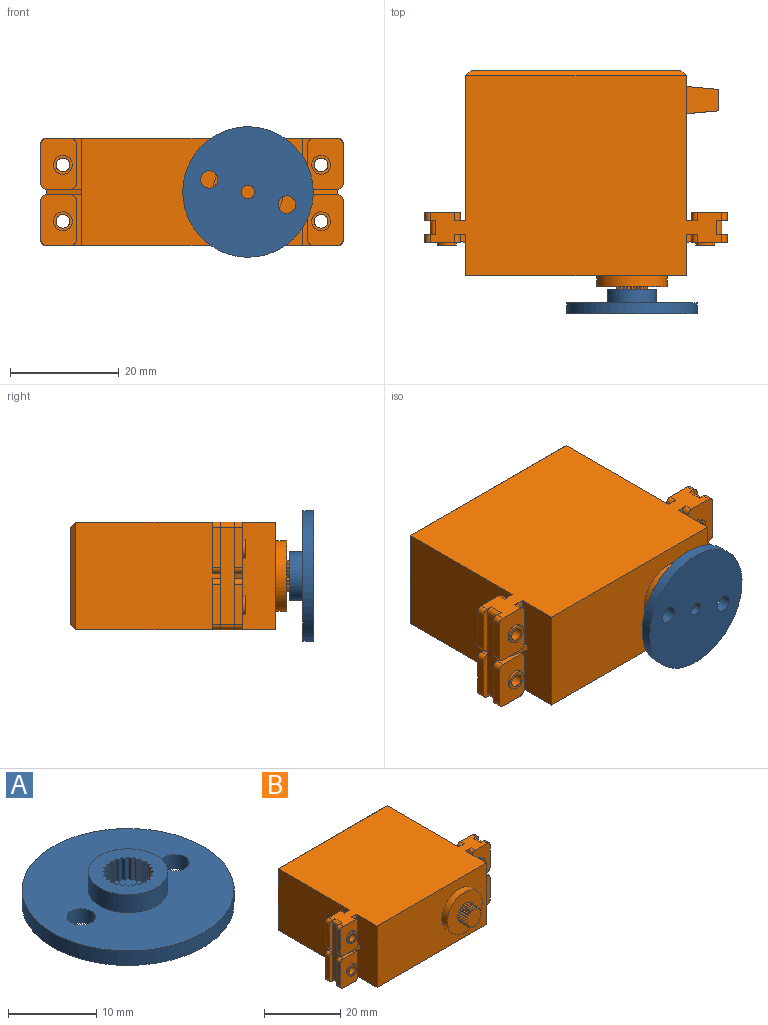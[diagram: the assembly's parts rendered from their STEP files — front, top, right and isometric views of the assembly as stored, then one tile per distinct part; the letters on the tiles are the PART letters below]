
ASSEMBLY  parts=2 mates=1
PART A: 57 faces, bbox 24x24x4.5 mm
  f0: plane 9x9mm, normal (0,0,1), area 40.5mm2, adj f4,f6,f7,f8,f9,f10,f11,f12
  f1: cylinder r=12mm len=24mm, axis (0,0,-1), area 150.8mm2, adj f2,f3
  f2: plane 24x24mm, normal (0,0,1), area 372.7mm2, adj f1,f4,f55,f56
  f3: plane 24x24mm, normal (0,0,-1), area 431.4mm2, adj f1,f54,f55,f56
  f4: cylinder r=4.5mm len=9mm, axis (0,0,-1), area 70.7mm2, adj f0,f2
  f5: plane 5.76x5.76mm, normal (0,0,1), area 18.2mm2, adj f6,f7,f8,f9,f10,f11,f12,f13
  f6: plane 3x0.34mm, normal (-0.71,-0.7,0), area 1.4mm2, adj f0,f5,f7,f9
  f7: plane 3x0.34mm, normal (0.71,-0.7,0), area 1.4mm2, adj f0,f5,f6,f52
  f8: plane 3x0.41mm, normal (-0.87,-0.5,0), area 1.4mm2, adj f0,f5,f9,f11
  f9: plane 3x0.41mm, normal (0.5,-0.86,0), area 1.4mm2, adj f0,f5,f6,f8
  f10: plane 3x0.46mm, normal (-0.97,-0.26,0), area 1.4mm2, adj f0,f5,f11,f13
  f11: plane 3x0.46mm, normal (0.26,-0.97,0), area 1.4mm2, adj f0,f5,f8,f10
  f12: plane 3x0.48mm, normal (-1,0,0), area 1.4mm2, adj f0,f5,f13,f15
  f13: plane 3x0.48mm, normal (0,-1,0), area 1.4mm2, adj f0,f5,f10,f12
  f14: plane 3x0.46mm, normal (-0.97,0.26,0), area 1.4mm2, adj f0,f5,f15,f17
  f15: plane 3x0.46mm, normal (-0.26,-0.97,0), area 1.4mm2, adj f0,f5,f12,f14
  f16: plane 3x0.41mm, normal (-0.86,0.5,0), area 1.4mm2, adj f0,f5,f17,f19
  f17: plane 3x0.41mm, normal (-0.5,-0.87,0), area 1.4mm2, adj f0,f5,f14,f16
  f18: plane 3x0.34mm, normal (-0.7,0.71,0), area 1.4mm2, adj f0,f5,f19,f21
  f19: plane 3x0.34mm, normal (-0.7,-0.71,0), area 1.4mm2, adj f0,f5,f16,f18
  f20: plane 3x0.41mm, normal (-0.5,0.87,0), area 1.4mm2, adj f0,f5,f21,f23
  f21: plane 3x0.41mm, normal (-0.86,-0.5,0), area 1.4mm2, adj f0,f5,f18,f20
  f22: plane 3x0.46mm, normal (-0.26,0.97,0), area 1.4mm2, adj f0,f5,f23,f25
  f23: plane 3x0.46mm, normal (-0.97,-0.26,0), area 1.4mm2, adj f0,f5,f20,f22
  f24: plane 3x0.48mm, normal (0,1,0), area 1.4mm2, adj f0,f5,f25,f27
  f25: plane 3x0.48mm, normal (-1,0,0), area 1.4mm2, adj f0,f5,f22,f24
  f26: plane 3x0.46mm, normal (0.26,0.97,0), area 1.4mm2, adj f0,f5,f27,f29
  f27: plane 3x0.46mm, normal (-0.97,0.26,0), area 1.4mm2, adj f0,f5,f24,f26
  f28: plane 3x0.41mm, normal (0.5,0.86,0), area 1.4mm2, adj f0,f5,f29,f31
  f29: plane 3x0.41mm, normal (-0.87,0.5,0), area 1.4mm2, adj f0,f5,f26,f28
  f30: plane 3x0.34mm, normal (0.71,0.7,0), area 1.4mm2, adj f0,f5,f31,f33
  f31: plane 3x0.34mm, normal (-0.71,0.7,0), area 1.4mm2, adj f0,f5,f28,f30
  f32: plane 3x0.41mm, normal (0.87,0.5,0), area 1.4mm2, adj f0,f5,f33,f35
  f33: plane 3x0.41mm, normal (-0.5,0.86,0), area 1.4mm2, adj f0,f5,f30,f32
  f34: plane 3x0.46mm, normal (0.97,0.26,0), area 1.4mm2, adj f0,f5,f35,f37
  f35: plane 3x0.46mm, normal (-0.26,0.97,0), area 1.4mm2, adj f0,f5,f32,f34
  f36: plane 3x0.48mm, normal (1,0,0), area 1.4mm2, adj f0,f5,f37,f39
  f37: plane 3x0.48mm, normal (0,1,0), area 1.4mm2, adj f0,f5,f34,f36
  f38: plane 3x0.46mm, normal (0.97,-0.26,0), area 1.4mm2, adj f0,f5,f39,f41
  f39: plane 3x0.46mm, normal (0.26,0.97,0), area 1.4mm2, adj f0,f5,f36,f38
  f40: plane 3x0.41mm, normal (0.86,-0.5,0), area 1.4mm2, adj f0,f5,f41,f43
  f41: plane 3x0.41mm, normal (0.5,0.87,0), area 1.4mm2, adj f0,f5,f38,f40
  f42: plane 3x0.34mm, normal (0.7,-0.71,0), area 1.4mm2, adj f0,f5,f43,f45
  f43: plane 3x0.34mm, normal (0.7,0.71,0), area 1.4mm2, adj f0,f5,f40,f42
  f44: plane 3x0.41mm, normal (0.5,-0.87,0), area 1.4mm2, adj f0,f5,f45,f47
  f45: plane 3x0.41mm, normal (0.86,0.5,0), area 1.4mm2, adj f0,f5,f42,f44
  f46: plane 3x0.46mm, normal (0.26,-0.97,0), area 1.4mm2, adj f0,f5,f47,f49
  f47: plane 3x0.46mm, normal (0.97,0.26,0), area 1.4mm2, adj f0,f5,f44,f46
  f48: plane 3x0.48mm, normal (0,-1,0), area 1.4mm2, adj f0,f5,f49,f51
  f49: plane 3x0.48mm, normal (1,0,0), area 1.4mm2, adj f0,f5,f46,f48
  f50: plane 3x0.46mm, normal (-0.26,-0.97,0), area 1.4mm2, adj f0,f5,f51,f53
  f51: plane 3x0.46mm, normal (0.97,-0.26,0), area 1.4mm2, adj f0,f5,f48,f50
  f52: plane 3x0.41mm, normal (-0.5,-0.86,0), area 1.4mm2, adj f0,f5,f7,f53
  f53: plane 3x0.41mm, normal (0.87,-0.5,0), area 1.4mm2, adj f0,f5,f50,f52
  f54: cylinder r=1.25mm len=2.5mm, axis (0,0,-1), area 11.8mm2, adj f3,f5
  f55: cylinder r=1.6mm len=3.2mm, axis (0,0,-1), area 20.1mm2, adj f2,f3
  f56: cylinder r=1.6mm len=3.2mm, axis (0,0,-1), area 20.1mm2, adj f2,f3
PART B: 178 faces, bbox 55.6x43.3x19.8 mm
  f0: plane 9.4x2mm, normal (0,-1,0), area 9.8mm2, adj f6,f11,f85,f155,f156,f157
  f1: plane 19.8x6.5mm, normal (0,1,0), area 26.2mm2, adj f8,f10,f11,f19,f138,f142,f143,f144
  f2: plane 9.4x2mm, normal (0,-1,0), area 9.8mm2, adj f4,f7,f11,f112,f113,f114
  f3: plane 19.8x6.5mm, normal (0,1,0), area 26.2mm2, adj f9,f10,f11,f15,f96,f100,f101,f102
  f4: plane 2x1.5mm, normal (0,0,-1), area 2.5mm2, adj f2,f7,f82,f112
  f5: plane 2x1.5mm, normal (0,0,1), area 2.5mm2, adj f7,f14,f82,f94
  f6: plane 19.8x7.6mm, normal (-1,0,0), area 149mm2, adj f0,f10,f11,f12,f18,f83,f84,f85
  f7: plane 19.8x7.6mm, normal (1,0,0), area 149mm2, adj f2,f4,f5,f10,f11,f12,f14,f82
  f8: plane 26.6x19.8mm, normal (-1,0,0), area 526.7mm2, adj f1,f10,f11,f76
  f9: plane 26.6x19.8mm, normal (1,0,0), area 491.7mm2, adj f3,f10,f11,f73,f77,f78,f79,f80
  f10: plane 53.6x36.8mm, normal (0,0,1), area 1549.7mm2, adj f1,f3,f6,f7,f8,f9,f12,f14
  f11: plane 53.6x36.8mm, normal (0,0,-1), area 1549.7mm2, adj f0,f1,f2,f3,f6,f7,f8,f9
  f12: plane 40.6x19.8mm, normal (0,-1,0), area 671.1mm2, adj f6,f7,f10,f11,f22
  f13: plane 38.6x17.8mm, normal (0,1,0), area 687.1mm2, adj f73,f74,f75,f76
  f14: plane 9.4x2mm, normal (0,-1,0), area 9.8mm2, adj f5,f7,f10,f92,f93,f94
  f15: plane 17.8x2.6mm, normal (1,0,0), area 46.3mm2, adj f3,f16,f17,f82,f87,f88,f107,f124
  f16: cylinder r=1mm len=2.6mm, axis (0,-1,0), area 4.1mm2, adj f10,f15,f87,f88
  f17: cylinder r=1mm len=2.6mm, axis (0,1,0), area 4.1mm2, adj f11,f15,f107,f124
  f18: plane 9.4x2mm, normal (0,-1,0), area 9.8mm2, adj f6,f10,f84,f134,f135,f136
  f19: plane 17.8x2.6mm, normal (-1,0,0), area 46.3mm2, adj f1,f20,f21,f83,f128,f137,f150,f158
  f20: cylinder r=1mm len=2.6mm, axis (0,-1,0), area 4.1mm2, adj f10,f19,f128,f137
  f21: cylinder r=1mm len=2.6mm, axis (0,1,0), area 4.1mm2, adj f11,f19,f150,f158
  f22: cylinder r=6.5mm len=13mm, axis (0,1,0), area 81.7mm2, adj f12,f23
  f23: plane 13x13mm, normal (0,-1,0), area 109.6mm2, adj f22,f25,f26,f27,f28,f29,f30,f31
  f24: plane 5.76x5.76mm, normal (0,-1,0), area 23.1mm2, adj f25,f26,f27,f28,f29,f30,f31,f32
  f25: plane 3.5x0.34mm, normal (0.71,0,0.7), area 1.7mm2, adj f23,f24,f26,f28
  f26: plane 3.5x0.34mm, normal (-0.71,0,0.7), area 1.7mm2, adj f23,f24,f25,f71
  f27: plane 3.5x0.41mm, normal (0.87,0,0.5), area 1.7mm2, adj f23,f24,f28,f30
  f28: plane 3.5x0.41mm, normal (-0.5,0,0.86), area 1.7mm2, adj f23,f24,f25,f27
  f29: plane 3.5x0.46mm, normal (0.97,0,0.26), area 1.7mm2, adj f23,f24,f30,f32
  f30: plane 3.5x0.46mm, normal (-0.26,0,0.97), area 1.7mm2, adj f23,f24,f27,f29
  f31: plane 3.5x0.48mm, normal (1,0,0), area 1.7mm2, adj f23,f24,f32,f34
  f32: plane 3.5x0.48mm, normal (0,0,1), area 1.7mm2, adj f23,f24,f29,f31
  f33: plane 3.5x0.46mm, normal (0.97,0,-0.26), area 1.7mm2, adj f23,f24,f34,f36
  f34: plane 3.5x0.46mm, normal (0.26,0,0.97), area 1.7mm2, adj f23,f24,f31,f33
  f35: plane 3.5x0.41mm, normal (0.86,0,-0.5), area 1.7mm2, adj f23,f24,f36,f38
  f36: plane 3.5x0.41mm, normal (0.5,0,0.87), area 1.7mm2, adj f23,f24,f33,f35
  f37: plane 3.5x0.34mm, normal (0.7,0,-0.71), area 1.7mm2, adj f23,f24,f38,f40
  f38: plane 3.5x0.34mm, normal (0.7,0,0.71), area 1.7mm2, adj f23,f24,f35,f37
  f39: plane 3.5x0.41mm, normal (0.5,0,-0.87), area 1.7mm2, adj f23,f24,f40,f42
  f40: plane 3.5x0.41mm, normal (0.86,0,0.5), area 1.7mm2, adj f23,f24,f37,f39
  f41: plane 3.5x0.46mm, normal (0.26,0,-0.97), area 1.7mm2, adj f23,f24,f42,f44
  f42: plane 3.5x0.46mm, normal (0.97,0,0.26), area 1.7mm2, adj f23,f24,f39,f41
  f43: plane 3.5x0.48mm, normal (0,0,-1), area 1.7mm2, adj f23,f24,f44,f46
  f44: plane 3.5x0.48mm, normal (1,0,0), area 1.7mm2, adj f23,f24,f41,f43
  f45: plane 3.5x0.46mm, normal (-0.26,0,-0.97), area 1.7mm2, adj f23,f24,f46,f48
  f46: plane 3.5x0.46mm, normal (0.97,0,-0.26), area 1.7mm2, adj f23,f24,f43,f45
  f47: plane 3.5x0.41mm, normal (-0.5,0,-0.86), area 1.7mm2, adj f23,f24,f48,f50
  f48: plane 3.5x0.41mm, normal (0.87,0,-0.5), area 1.7mm2, adj f23,f24,f45,f47
  f49: plane 3.5x0.34mm, normal (-0.71,0,-0.7), area 1.7mm2, adj f23,f24,f50,f52
  f50: plane 3.5x0.34mm, normal (0.71,0,-0.7), area 1.7mm2, adj f23,f24,f47,f49
  f51: plane 3.5x0.41mm, normal (-0.87,0,-0.5), area 1.7mm2, adj f23,f24,f52,f54
  f52: plane 3.5x0.41mm, normal (0.5,0,-0.86), area 1.7mm2, adj f23,f24,f49,f51
  f53: plane 3.5x0.46mm, normal (-0.97,0,-0.26), area 1.7mm2, adj f23,f24,f54,f56
  f54: plane 3.5x0.46mm, normal (0.26,0,-0.97), area 1.7mm2, adj f23,f24,f51,f53
  f55: plane 3.5x0.48mm, normal (-1,0,0), area 1.7mm2, adj f23,f24,f56,f58
  f56: plane 3.5x0.48mm, normal (0,0,-1), area 1.7mm2, adj f23,f24,f53,f55
  f57: plane 3.5x0.46mm, normal (-0.97,0,0.26), area 1.7mm2, adj f23,f24,f58,f60
  f58: plane 3.5x0.46mm, normal (-0.26,0,-0.97), area 1.7mm2, adj f23,f24,f55,f57
  f59: plane 3.5x0.41mm, normal (-0.86,0,0.5), area 1.7mm2, adj f23,f24,f60,f62
  f60: plane 3.5x0.41mm, normal (-0.5,0,-0.87), area 1.7mm2, adj f23,f24,f57,f59
  f61: plane 3.5x0.34mm, normal (-0.7,0,0.71), area 1.7mm2, adj f23,f24,f62,f64
  f62: plane 3.5x0.34mm, normal (-0.7,0,-0.71), area 1.7mm2, adj f23,f24,f59,f61
  f63: plane 3.5x0.41mm, normal (-0.5,0,0.87), area 1.7mm2, adj f23,f24,f64,f66
  f64: plane 3.5x0.41mm, normal (-0.86,0,-0.5), area 1.7mm2, adj f23,f24,f61,f63
  f65: plane 3.5x0.46mm, normal (-0.26,0,0.97), area 1.7mm2, adj f23,f24,f66,f68
  f66: plane 3.5x0.46mm, normal (-0.97,0,-0.26), area 1.7mm2, adj f23,f24,f63,f65
  f67: plane 3.5x0.48mm, normal (0,0,1), area 1.7mm2, adj f23,f24,f68,f70
  f68: plane 3.5x0.48mm, normal (-1,0,0), area 1.7mm2, adj f23,f24,f65,f67
  f69: plane 3.5x0.46mm, normal (0.26,0,0.97), area 1.7mm2, adj f23,f24,f70,f72
  f70: plane 3.5x0.46mm, normal (-0.97,0,0.26), area 1.7mm2, adj f23,f24,f67,f69
  f71: plane 3.5x0.41mm, normal (0.5,0,0.86), area 1.7mm2, adj f23,f24,f26,f72
  f72: plane 3.5x0.41mm, normal (-0.87,0,0.5), area 1.7mm2, adj f23,f24,f69,f71
  f73: plane 19.8x1mm, normal (0.71,0.71,0), area 26.6mm2, adj f9,f13,f74,f75
  f74: plane 40.6x1mm, normal (0,0.71,-0.71), area 56mm2, adj f11,f13,f73,f76
  f75: plane 40.6x1mm, normal (0,0.71,0.71), area 56mm2, adj f10,f13,f73,f76
  f76: plane 19.8x1mm, normal (-0.71,0.71,0), area 26.6mm2, adj f8,f13,f74,f75
  f77: plane 6x5mm, normal (0.09,0,-1), area 27mm2, adj f9,f78,f80,f81
  f78: plane 7x6mm, normal (0.09,1,0), area 39mm2, adj f9,f77,f79,f81
  f79: plane 6x5mm, normal (0.09,0,1), area 27mm2, adj f9,f78,f80,f81
  f80: plane 7x6mm, normal (0.09,-1,0), area 39mm2, adj f9,f77,f79,f81
  f81: plane 5.95x3.95mm, normal (1,0,0), area 23.5mm2, adj f77,f78,f79,f80
  f82: plane 6.5x1.5mm, normal (0.22,-0.97,0), area 6.7mm2, adj f4,f5,f7,f15,f86,f111
  f83: plane 6.5x1.5mm, normal (-0.22,-0.97,0), area 6.7mm2, adj f6,f19,f84,f85,f130,f149
  f84: plane 2x1.5mm, normal (0,0,1), area 2.5mm2, adj f6,f18,f83,f136
  f85: plane 2x1.5mm, normal (0,0,-1), area 2.5mm2, adj f0,f6,f83,f155
  f86: plane 4.5x1.5mm, normal (0,0,-1), area 4.4mm2, adj f82,f89,f94,f95
  f87: plane 9.4x2mm, normal (0,-1,0), area 9.2mm2, adj f10,f15,f16,f97,f98,f99
  f88: plane 9.4x2mm, normal (0,1,0), area 9.2mm2, adj f10,f15,f16,f89,f90,f91
  f89: cylinder r=1mm len=1.5mm, axis (0,1,0), area 2.4mm2, adj f86,f88,f90,f95
  f90: plane 7.4x1.5mm, normal (1,0,0), area 11.1mm2, adj f88,f89,f91,f95
  f91: cylinder r=1mm len=1.5mm, axis (0,1,0), area 2.4mm2, adj f10,f88,f90,f95
  f92: cylinder r=1mm len=1.5mm, axis (0,1,0), area 2.4mm2, adj f10,f14,f93,f95
  f93: plane 7.4x1.5mm, normal (-1,0,0), area 11.1mm2, adj f14,f92,f94,f95
  f94: cylinder r=1mm len=1.5mm, axis (0,1,0), area 2.4mm2, adj f5,f14,f86,f93,f95
  f95: plane 9.4x6.5mm, normal (0,-1,0), area 50.6mm2, adj f10,f86,f89,f90,f91,f92,f93,f94
  f96: cylinder r=1mm len=1.5mm, axis (0,-1,0), area 2.4mm2, adj f3,f10,f102,f103
  f97: cylinder r=1mm len=1.5mm, axis (0,-1,0), area 2.4mm2, adj f10,f87,f98,f103
  f98: plane 7.4x1.5mm, normal (1,0,0), area 11.1mm2, adj f87,f97,f99,f103
  f99: cylinder r=1mm len=1.5mm, axis (0,-1,0), area 2.4mm2, adj f87,f98,f100,f103
  f100: plane 4.5x1.5mm, normal (0,0,-1), area 6.7mm2, adj f3,f99,f101,f103
  f101: cylinder r=1mm len=1.5mm, axis (0,-1,0), area 2.4mm2, adj f3,f100,f102,f103
  f102: plane 7.4x1.5mm, normal (-1,0,0), area 11.1mm2, adj f3,f96,f101,f103
  f103: plane 9.4x6.5mm, normal (0,1,0), area 55.3mm2, adj f10,f96,f97,f98,f99,f100,f101,f102
  f104: cylinder r=1.25mm len=6.1mm, axis (0,-1,0), area 47.9mm2, adj f103,f106
  f105: cylinder r=1.75mm len=3.5mm, axis (0,1,0), area 5.5mm2, adj f95,f106
  f106: plane 3.5x3.5mm, normal (0,-1,0), area 4.7mm2, adj f104,f105
  f107: plane 9.4x2mm, normal (0,1,0), area 9.2mm2, adj f11,f15,f17,f108,f109,f110
  f108: cylinder r=1mm len=1.5mm, axis (0,1,0), area 2.4mm2, adj f11,f107,f109,f115
  f109: plane 7.4x1.5mm, normal (1,0,0), area 11.1mm2, adj f107,f108,f110,f115
  f110: cylinder r=1mm len=1.5mm, axis (0,1,0), area 2.4mm2, adj f107,f109,f111,f115
  f111: plane 4.5x1.5mm, normal (0,0,1), area 4.4mm2, adj f82,f110,f112,f115
  f112: cylinder r=1mm len=1.5mm, axis (0,1,0), area 2.4mm2, adj f2,f4,f111,f113,f115
  f113: plane 7.4x1.5mm, normal (-1,0,0), area 11.1mm2, adj f2,f112,f114,f115
  f114: cylinder r=1mm len=1.5mm, axis (0,1,0), area 2.4mm2, adj f2,f11,f113,f115
  f115: plane 9.4x6.5mm, normal (0,-1,0), area 50.6mm2, adj f11,f108,f109,f110,f111,f112,f113,f114
  f116: cylinder r=1mm len=1.5mm, axis (0,-1,0), area 2.4mm2, adj f3,f117,f122,f123
  f117: plane 4.5x1.5mm, normal (0,0,1), area 6.7mm2, adj f3,f116,f118,f123
  f118: cylinder r=1mm len=1.5mm, axis (0,-1,0), area 2.4mm2, adj f117,f119,f123,f124
  f119: plane 7.4x1.5mm, normal (1,0,0), area 11.1mm2, adj f118,f120,f123,f124
  f120: cylinder r=1mm len=1.5mm, axis (0,-1,0), area 2.4mm2, adj f11,f119,f123,f124
  f121: cylinder r=1mm len=1.5mm, axis (0,-1,0), area 2.4mm2, adj f3,f11,f122,f123
  f122: plane 7.4x1.5mm, normal (-1,0,0), area 11.1mm2, adj f3,f116,f121,f123
  f123: plane 9.4x6.5mm, normal (0,1,0), area 55.3mm2, adj f11,f116,f117,f118,f119,f120,f121,f122
  f124: plane 9.4x2mm, normal (0,-1,0), area 9.2mm2, adj f11,f15,f17,f118,f119,f120
  f125: cylinder r=1.25mm len=6.1mm, axis (0,-1,0), area 47.9mm2, adj f123,f127
  f126: cylinder r=1.75mm len=3.5mm, axis (0,1,0), area 5.5mm2, adj f115,f127
  f127: plane 3.5x3.5mm, normal (0,-1,0), area 4.7mm2, adj f125,f126
  f128: plane 9.4x2mm, normal (0,-1,0), area 9.2mm2, adj f10,f19,f20,f139,f140,f141
  f129: plane 9.4x6.5mm, normal (0,-1,0), area 50.6mm2, adj f10,f130,f131,f132,f133,f134,f135,f136
  f130: plane 4.5x1.5mm, normal (0,0,-1), area 4.4mm2, adj f83,f129,f131,f136
  f131: cylinder r=1mm len=1.5mm, axis (0,1,0), area 2.4mm2, adj f129,f130,f132,f137
  f132: plane 7.4x1.5mm, normal (-1,0,0), area 11.1mm2, adj f129,f131,f133,f137
  f133: cylinder r=1mm len=1.5mm, axis (0,1,0), area 2.4mm2, adj f10,f129,f132,f137
  f134: cylinder r=1mm len=1.5mm, axis (0,1,0), area 2.4mm2, adj f10,f18,f129,f135
  f135: plane 7.4x1.5mm, normal (1,0,0), area 11.1mm2, adj f18,f129,f134,f136
  f136: cylinder r=1mm len=1.5mm, axis (0,1,0), area 2.4mm2, adj f18,f84,f129,f130,f135
  f137: plane 9.4x2mm, normal (0,1,0), area 9.2mm2, adj f10,f19,f20,f131,f132,f133
  f138: cylinder r=1mm len=1.5mm, axis (0,-1,0), area 2.4mm2, adj f1,f10,f144,f145
  f139: cylinder r=1mm len=1.5mm, axis (0,-1,0), area 2.4mm2, adj f10,f128,f140,f145
  f140: plane 7.4x1.5mm, normal (-1,0,0), area 11.1mm2, adj f128,f139,f141,f145
  f141: cylinder r=1mm len=1.5mm, axis (0,-1,0), area 2.4mm2, adj f128,f140,f142,f145
  f142: plane 4.5x1.5mm, normal (0,0,-1), area 6.7mm2, adj f1,f141,f143,f145
  f143: cylinder r=1mm len=1.5mm, axis (0,-1,0), area 2.4mm2, adj f1,f142,f144,f145
  f144: plane 7.4x1.5mm, normal (1,0,0), area 11.1mm2, adj f1,f138,f143,f145
  f145: plane 9.4x6.5mm, normal (0,1,0), area 55.3mm2, adj f10,f138,f139,f140,f141,f142,f143,f144
  f146: cylinder r=1.25mm len=6.1mm, axis (0,-1,0), area 47.9mm2, adj f145,f148
  f147: cylinder r=1.75mm len=3.5mm, axis (0,1,0), area 5.5mm2, adj f129,f148
  f148: plane 3.5x3.5mm, normal (0,-1,0), area 4.7mm2, adj f146,f147
  f149: plane 4.5x1.5mm, normal (0,0,1), area 4.4mm2, adj f83,f151,f154,f155
  f150: plane 9.4x2mm, normal (0,-1,0), area 9.2mm2, adj f11,f19,f21,f161,f162,f163
  f151: plane 9.4x6.5mm, normal (0,-1,0), area 50.6mm2, adj f11,f149,f152,f153,f154,f155,f156,f157
  f152: cylinder r=1mm len=1.5mm, axis (0,1,0), area 2.4mm2, adj f11,f151,f153,f158
  f153: plane 7.4x1.5mm, normal (-1,0,0), area 11.1mm2, adj f151,f152,f154,f158
  f154: cylinder r=1mm len=1.5mm, axis (0,1,0), area 2.4mm2, adj f149,f151,f153,f158
  f155: cylinder r=1mm len=1.5mm, axis (0,1,0), area 2.4mm2, adj f0,f85,f149,f151,f156
  f156: plane 7.4x1.5mm, normal (1,0,0), area 11.1mm2, adj f0,f151,f155,f157
  f157: cylinder r=1mm len=1.5mm, axis (0,1,0), area 2.4mm2, adj f0,f11,f151,f156
  f158: plane 9.4x2mm, normal (0,1,0), area 9.2mm2, adj f11,f19,f21,f152,f153,f154
  f159: cylinder r=1mm len=1.5mm, axis (0,-1,0), area 2.4mm2, adj f1,f160,f165,f166
  f160: plane 4.5x1.5mm, normal (0,0,1), area 6.7mm2, adj f1,f159,f161,f166
  f161: cylinder r=1mm len=1.5mm, axis (0,-1,0), area 2.4mm2, adj f150,f160,f162,f166
  f162: plane 7.4x1.5mm, normal (-1,0,0), area 11.1mm2, adj f150,f161,f163,f166
  f163: cylinder r=1mm len=1.5mm, axis (0,-1,0), area 2.4mm2, adj f11,f150,f162,f166
  f164: cylinder r=1mm len=1.5mm, axis (0,-1,0), area 2.4mm2, adj f1,f11,f165,f166
  f165: plane 7.4x1.5mm, normal (1,0,0), area 11.1mm2, adj f1,f159,f164,f166
  f166: plane 9.4x6.5mm, normal (0,1,0), area 55.3mm2, adj f11,f159,f160,f161,f162,f163,f164,f165
  f167: cylinder r=1.25mm len=6.1mm, axis (0,-1,0), area 47.9mm2, adj f166,f169
  f168: cylinder r=1.75mm len=3.5mm, axis (0,1,0), area 5.5mm2, adj f151,f169
  f169: plane 3.5x3.5mm, normal (0,-1,0), area 4.7mm2, adj f167,f168
  f170: cylinder r=2.2mm len=4.38mm, axis (0,-1,0), area 16.9mm2, adj f171,f172,f173
  f171: plane 4.4x2.4mm, normal (0,-1,0), area 1.8mm2, adj f170,f173
  f172: plane 4.4x2.4mm, normal (0,1,0), area 1.8mm2, adj f170,f173
  f173: cylinder r=2.2mm len=4.4mm, axis (0,-1,0), area 19mm2, adj f170,f171,f172
  f174: cylinder r=2.2mm len=4.4mm, axis (0,-1,0), area 19mm2, adj f175,f176,f177
  f175: cylinder r=2.2mm len=4.38mm, axis (0,-1,0), area 16.9mm2, adj f174,f176,f177
  f176: plane 4.4x2.4mm, normal (0,-1,0), area 1.8mm2, adj f174,f175
  f177: plane 4.4x2.4mm, normal (0,1,0), area 1.8mm2, adj f174,f175
PLACE A rot(axis=(-0.98,0.15,0.15),91.4deg) t=(10.3,-44.8,0)mm
PLACE B at identity fixed
MATE revolute B.f22 <-> A.f1  axis (0,-1,0) through (10.3,-43.3,0)mm
